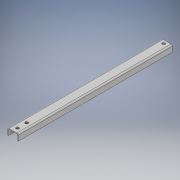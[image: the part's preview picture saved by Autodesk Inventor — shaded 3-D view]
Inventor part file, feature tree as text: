
AUTODESK INVENTOR PART (.ipt)
format: ipt  version: 2019 (Build 230136000, 136)  size: 140,800 bytes
history: native  units: mm
features: other x5, sketch x4, hole x2, sheet_metal_op x1
ambient origin geometry x8: Origin, YZ Plane, XZ Plane, XY Plane, X Axis, Y Axis, Z Axis, Center Point
bodies: Body1 (feature_tree)
feature tree (12):
  sheet_metal_op  "Face2"
  other  "Bord tombé2"
  hole  "Perçage2"  [1 undecoded]
  hole  "Perçage3"  [1 undecoded]
  sketch  "Esquisse4"
  other  "Plaque3"
  sketch  "Esquisse5"
  other  "Plaque4"
  other  "Pli2"
  other  "Coin2"
  sketch  "Esquisse6"
  sketch  "Esquisse7"
note: 2 required parameter values undecoded (feature->parameter linkage not recoverable at this tier; creation-order binding heuristic only, values carry confidence <= 0.55)
